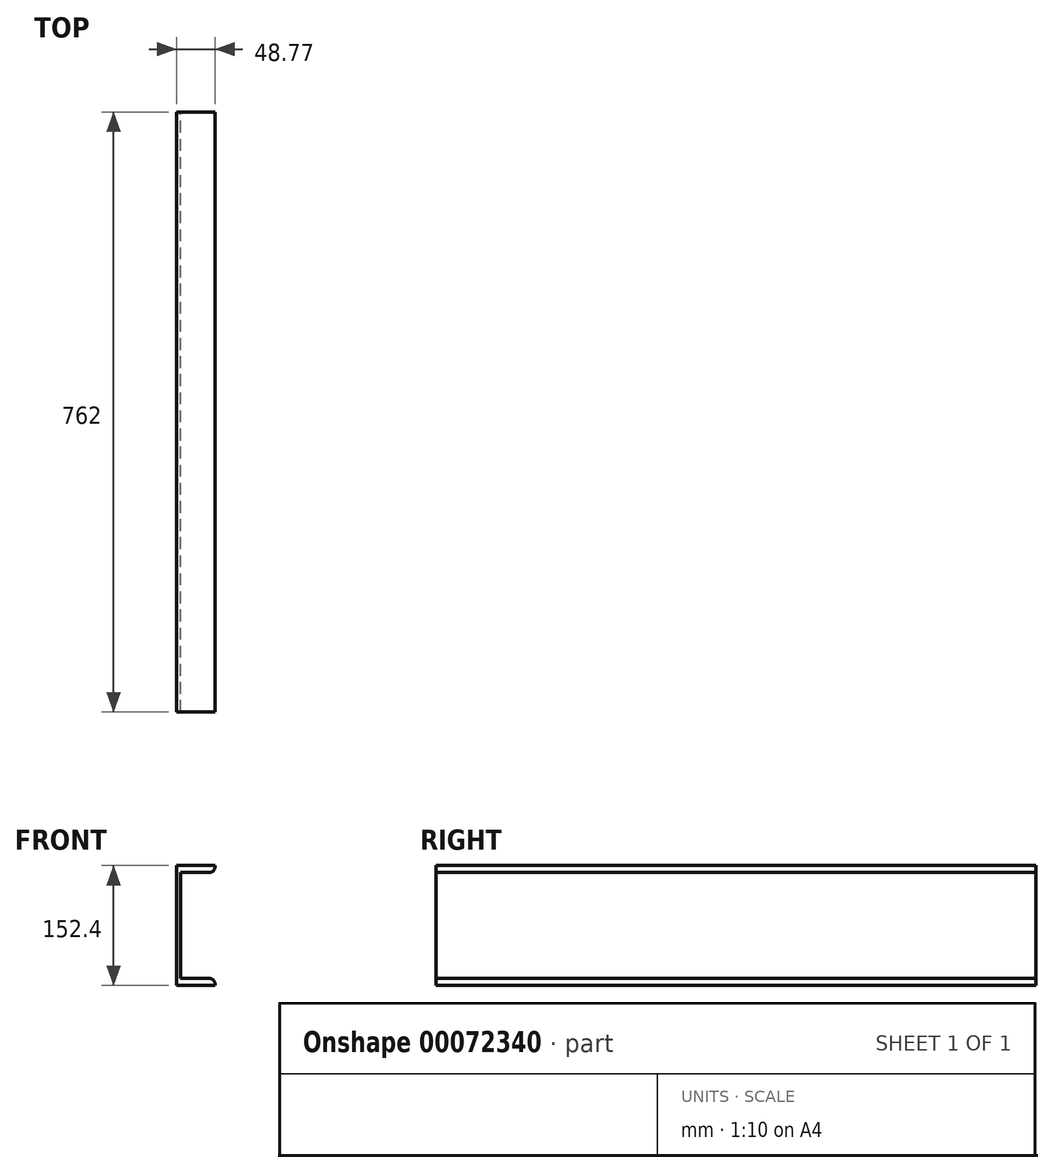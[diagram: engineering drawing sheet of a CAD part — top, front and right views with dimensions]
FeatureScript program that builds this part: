
annotation { "Feature Type Name" : "Feature", "Feature Type Description" : "" }
export const myFeature = defineFeature(function(context is Context, id is Id, definition is map)
    precondition{}
    {
        {
            var Q0;
            Q0=qCreatedBy(makeId("Front.planeOp"),FACE);
            var sketch = newSketch(context, id + "F0", { "sketchPlane" : qUnion([Q0])});
            skLineSegment(sketch, "E0", {"start": v(-31.5, 72.68) * mm, "end": v(-31.5, -72.31) * mm});
            skLineSegment(sketch, "E1", {"start": v(-31.5, -72.31) * mm, "end": v(17.27, -72.31) * mm});
            skLineSegment(sketch, "E2", {"start": v(17.27, -72.31) * mm, "end": v(17.27, -69.95) * mm});
            skLineSegment(sketch, "E3", {"start": v(10.92, -63.6) * mm, "end": v(-26.42, -63.6) * mm});
            skLineSegment(sketch, "E4", {"start": v(-26.42, -63.6) * mm, "end": v(-26.42, 71.38) * mm});
            skLineSegment(sketch, "E5", {"start": v(-26.42, 71.38) * mm, "end": v(10.92, 71.38) * mm});
            skLineSegment(sketch, "E6", {"start": v(17.27, 77.73) * mm, "end": v(17.27, 80.09) * mm});
            skLineSegment(sketch, "E7", {"start": v(17.27, 80.09) * mm, "end": v(-31.5, 80.09) * mm});
            skLineSegment(sketch, "E8", {"start": v(-31.5, 72.68) * mm, "end": v(-31.5, 80.09) * mm});
            skPoint(sketch, "E9.visualSharp", {"position": v(17.27, -63.6) * mm});
            skArc(sketch, "E9.filletArc", {"start": v(17.27, -69.95) * mm, "mid": v(15.4, -65.46) * mm, "end": v(10.92, -63.6) * mm});
            skPoint(sketch, "E10.visualSharp", {"position": v(17.27, 71.38) * mm});
            skArc(sketch, "E10.filletArc", {"start": v(10.92, 71.38) * mm, "mid": v(15.4, 73.24) * mm, "end": v(17.27, 77.73) * mm});
            skSolve(sketch);
        }
        {
            var Q0;
            Q0=makeQuery(id+"F0.imprint","IMPRINT",FACE,{"disambiguationData":[TD([[makeQuery(id+"F0.imprint","IMPRINT",EDGE,{"derivedFrom":sQuery(id+"F0.wireOp",EDGE,"E0")}),1.0]])]});
            extrude(context, id + "F1", {"entities" : qUnion([Q0]), "depth" : 762 * mm});
        }
    });
